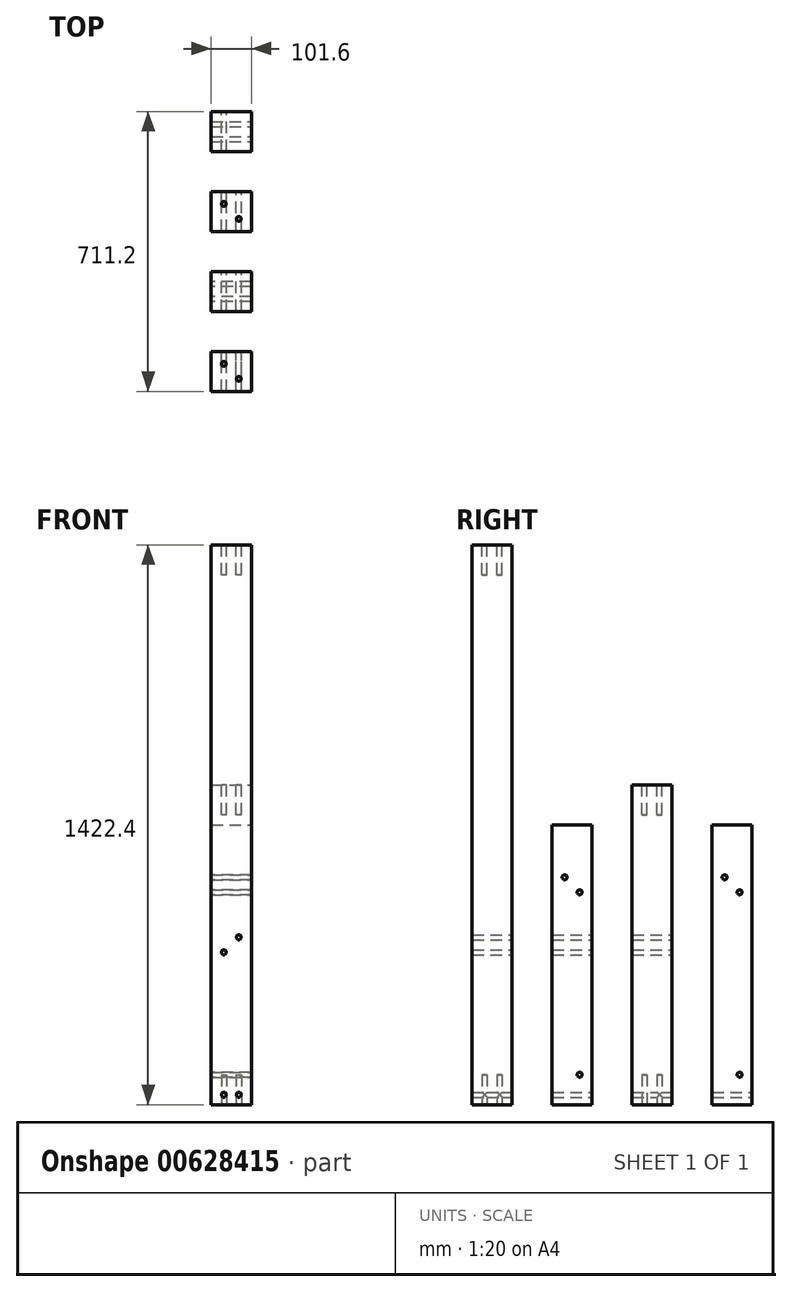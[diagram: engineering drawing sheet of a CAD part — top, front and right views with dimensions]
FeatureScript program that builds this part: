
annotation { "Feature Type Name" : "Feature", "Feature Type Description" : "" }
export const myFeature = defineFeature(function(context is Context, id is Id, definition is map)
    precondition{}
    {
        {
            var Q0;
            Q0=qCreatedBy(makeId("Top.planeOp"),FACE);
            var sketch = newSketch(context, id + "F0", { "sketchPlane" : qUnion([Q0])});
            skLineSegment(sketch, "E0", {"start": v(-50.8, 0) * mm, "end": v(50.8, 0) * mm});
            skLineSegment(sketch, "E1", {"start": v(50.8, 0) * mm, "end": v(50.8, 101.6) * mm});
            skLineSegment(sketch, "E2", {"start": v(50.8, 101.6) * mm, "end": v(-50.8, 101.6) * mm});
            skLineSegment(sketch, "E3", {"start": v(-50.8, 101.6) * mm, "end": v(-50.8, 0) * mm});
            skSolve(sketch);
        }
        {
            var Q0;
            Q0=makeQuery(id+"F0.imprint","IMPRINT",FACE,{"disambiguationData":[TD([[makeQuery(id+"F0.imprint","IMPRINT",EDGE,{"derivedFrom":sQuery(id+"F0.wireOp",EDGE,"E0")}),1.0]])]});
            extrude(context, id + "F1", {"entities" : qUnion([Q0]), "depth" : 711.2 * mm, "offsetDistance" : 25.4 * mm});
        }
        {
            var Q0;
            Q0=qCreatedBy(makeId("Top.planeOp"),FACE);
            var sketch = newSketch(context, id + "F2", { "sketchPlane" : qUnion([Q0])});
            skLineSegment(sketch, "E4", {"start": v(-50.8, -101.6) * mm, "end": v(50.8, -101.6) * mm});
            skLineSegment(sketch, "E5", {"start": v(50.8, -101.6) * mm, "end": v(50.8, -203.2) * mm});
            skLineSegment(sketch, "E6", {"start": v(50.8, -203.2) * mm, "end": v(-50.8, -203.2) * mm});
            skLineSegment(sketch, "E7", {"start": v(-50.8, -203.2) * mm, "end": v(-50.8, -101.6) * mm});
            skSolve(sketch);
        }
        {
            var Q0;
            Q0=makeQuery(id+"F2.imprint","IMPRINT",FACE,{"disambiguationData":[TD([[makeQuery(id+"F2.imprint","IMPRINT",EDGE,{"derivedFrom":sQuery(id+"F2.wireOp",EDGE,"E4")}),-1.0]])]});
            extrude(context, id + "F3", {"entities" : qUnion([Q0]), "depth" : 1422.4 * mm, "offsetDistance" : 25.4 * mm});
        }
        {
            var Q0;
            Q0=qCreatedBy(makeId("Top.planeOp"),FACE);
            var sketch = newSketch(context, id + "F4", { "sketchPlane" : qUnion([Q0])});
            skLineSegment(sketch, "E8.bottom", {"start": v(-50.8, 304.8) * mm, "end": v(50.8, 304.8) * mm});
            skLineSegment(sketch, "E8.top", {"start": v(-50.8, 203.2) * mm, "end": v(50.8, 203.2) * mm});
            skLineSegment(sketch, "E8.left", {"start": v(-50.8, 304.8) * mm, "end": v(-50.8, 203.2) * mm});
            skLineSegment(sketch, "E8.right", {"start": v(50.8, 304.8) * mm, "end": v(50.8, 203.2) * mm});
            skSolve(sketch);
        }
        {
            var Q0;
            Q0 = qSketchRegion(id + "F4", true);
            extrude(context, id + "F5", {"entities" : qUnion([Q0]), "depth" : 812.8 * mm, "offsetDistance" : 25.4 * mm});
        }
        {
            var Q0;
            Q0=makeQuery(id+"F1.opExtrude","SWEPT_FACE",FACE,{"disambiguationData":[OSD([sQuery(id+"F0.wireOp",EDGE,"E2")])]});
            var sketch = newSketch(context, id + "F6", { "sketchPlane" : qUnion([Q0])});
            skCircle(sketch, "E9", {"center": v(-19.05, 25.4) * mm, "radius": 6.35 * mm});
            skSolve(sketch);
        }
        {
            var Q0;
            Q0 = qSketchRegion(id + "F6", true);
            extrude(context, id + "F7", {"entities" : qUnion([Q0]), "operationType" : NewBodyOperationType.REMOVE, "endBound" : BoundingType.THROUGH_ALL, "oppositeDirection" : true, "depth" : 25.4 * mm, "offsetDistance" : 25.4 * mm});
        }
        {
            var Q0;
            Q0=makeQuery(id+"F1.opExtrude","SWEPT_FACE",FACE,{"disambiguationData":[OSD([sQuery(id+"F0.wireOp",EDGE,"E3")])]});
            var sketch = newSketch(context, id + "F8", { "sketchPlane" : qUnion([Q0])});
            skCircle(sketch, "E10", {"center": v(-69.85, 76.2) * mm, "radius": 6.35 * mm});
            skSolve(sketch);
        }
        {
            var Q0;
            Q0 = qSketchRegion(id + "F8", true);
            extrude(context, id + "F9", {"entities" : qUnion([Q0]), "operationType" : NewBodyOperationType.REMOVE, "endBound" : BoundingType.THROUGH_ALL, "oppositeDirection" : true, "depth" : 25.4 * mm, "offsetDistance" : 25.4 * mm});
        }
        {
            var Q0;
            Q0=makeQuery(id+"F1.opExtrude","SWEPT_FACE",FACE,{"disambiguationData":[OSD([sQuery(id+"F0.wireOp",EDGE,"E3")])]});
            var sketch = newSketch(context, id + "F10", { "sketchPlane" : qUnion([Q0])});
            skCircle(sketch, "E11", {"center": v(-31.75, 577.85) * mm, "radius": 6.35 * mm});
            skCircle(sketch, "E12", {"center": v(-69.85, 539.75) * mm, "radius": 6.35 * mm});
            skSolve(sketch);
        }
        {
            var Q0;
            Q0 = qSketchRegion(id + "F10", true);
            extrude(context, id + "F11", {"entities" : qUnion([Q0]), "operationType" : NewBodyOperationType.REMOVE, "endBound" : BoundingType.THROUGH_ALL, "oppositeDirection" : true, "depth" : 25.4 * mm, "offsetDistance" : 25.4 * mm});
        }
        {
            var Q0;
            Q0=makeQuery(id+"F3.opExtrude","CAP_FACE",FACE,{"disambiguationData":[OSD([sQuery(id+"F2.wireOp",EDGE,"E4"),sQuery(id+"F2.wireOp",EDGE,"E5"),sQuery(id+"F2.wireOp",EDGE,"E6"),sQuery(id+"F2.wireOp",EDGE,"E7")])],"isStart":true});
            var sketch = newSketch(context, id + "F12", { "sketchPlane" : qUnion([Q0])});
            skCircle(sketch, "E13", {"center": v(19.05, 171.45) * mm, "radius": 6.35 * mm});
            skCircle(sketch, "E14", {"center": v(-19.05, 133.35) * mm, "radius": 6.35 * mm});
            skSolve(sketch);
        }
        {
            var Q0;
            Q0 = qSketchRegion(id + "F12", true);
            extrude(context, id + "F13", {"entities" : qUnion([Q0]), "operationType" : NewBodyOperationType.REMOVE, "oppositeDirection" : true, "depth" : 76.2 * mm, "offsetDistance" : 25.4 * mm});
        }
        {
            var Q0;
            Q0=makeQuery(id+"F5.opExtrude","SWEPT_FACE",FACE,{"disambiguationData":[OSD([sQuery(id+"F4.wireOp",EDGE,"E8.bottom")])]});
            var sketch = newSketch(context, id + "F14", { "sketchPlane" : qUnion([Q0])});
            skPoint(sketch, "E15", {"position": v(0, 406.4) * mm});
            skPoint(sketch, "E15.positionSnap0", {"position": v(-50.8, 406.4) * mm});
            skPoint(sketch, "E15.positionSnap1", {"position": v(0, 0) * mm});
            skCircle(sketch, "E16", {"center": v(19.05, 387.35) * mm, "radius": 6.35 * mm});
            skCircle(sketch, "E17", {"center": v(-19.05, 425.45) * mm, "radius": 6.35 * mm});
            skSolve(sketch);
        }
        {
            var Q0;
            Q0 = qSketchRegion(id + "F14", true);
            extrude(context, id + "F15", {"entities" : qUnion([Q0]), "operationType" : NewBodyOperationType.REMOVE, "endBound" : BoundingType.THROUGH_ALL, "oppositeDirection" : true, "depth" : 25.4 * mm, "offsetDistance" : 25.4 * mm});
        }
        {
            var Q0;
            Q0=makeQuery(id+"F3.opExtrude","CAP_FACE",FACE,{"disambiguationData":[OSD([sQuery(id+"F2.wireOp",EDGE,"E4"),sQuery(id+"F2.wireOp",EDGE,"E5"),sQuery(id+"F2.wireOp",EDGE,"E6"),sQuery(id+"F2.wireOp",EDGE,"E7")])],"isStart":false});
            var sketch = newSketch(context, id + "F16", { "sketchPlane" : qUnion([Q0])});
            skCircle(sketch, "E18", {"center": v(-19.05, -133.35) * mm, "radius": 6.35 * mm});
            skCircle(sketch, "E19", {"center": v(19.05, -171.45) * mm, "radius": 6.35 * mm});
            skSolve(sketch);
        }
        {
            var Q0;
            Q0 = qSketchRegion(id + "F16", true);
            extrude(context, id + "F17", {"entities" : qUnion([Q0]), "operationType" : NewBodyOperationType.REMOVE, "oppositeDirection" : true, "depth" : 76.2 * mm, "offsetDistance" : 25.4 * mm});
        }
        {
            var Q0;
            Q0=makeQuery(id+"F5.opExtrude","CAP_FACE",FACE,{"disambiguationData":[OSD([sQuery(id+"F4.wireOp",EDGE,"E8.bottom"),sQuery(id+"F4.wireOp",EDGE,"E8.top"),sQuery(id+"F4.wireOp",EDGE,"E8.left"),sQuery(id+"F4.wireOp",EDGE,"E8.right")])],"isStart":false});
            var sketch = newSketch(context, id + "F18", { "sketchPlane" : qUnion([Q0])});
            skCircle(sketch, "E20", {"center": v(-19.05, 273.05) * mm, "radius": 6.35 * mm});
            skCircle(sketch, "E21", {"center": v(19.05, 234.95) * mm, "radius": 6.35 * mm});
            skSolve(sketch);
        }
        {
            var Q0;
            Q0 = qSketchRegion(id + "F18", true);
            extrude(context, id + "F19", {"entities" : qUnion([Q0]), "operationType" : NewBodyOperationType.REMOVE, "oppositeDirection" : true, "depth" : 76.2 * mm, "offsetDistance" : 25.4 * mm});
        }
        {
            var Q0;
            Q0=makeQuery(id+"F5.opExtrude","CAP_FACE",FACE,{"disambiguationData":[OSD([sQuery(id+"F4.wireOp",EDGE,"E8.bottom"),sQuery(id+"F4.wireOp",EDGE,"E8.top"),sQuery(id+"F4.wireOp",EDGE,"E8.left"),sQuery(id+"F4.wireOp",EDGE,"E8.right")])],"isStart":true});
            var sketch = newSketch(context, id + "F20", { "sketchPlane" : qUnion([Q0])});
            skCircle(sketch, "E22", {"center": v(19.05, -234.95) * mm, "radius": 6.35 * mm});
            skCircle(sketch, "E23", {"center": v(-19.05, -273.05) * mm, "radius": 6.35 * mm});
            skSolve(sketch);
        }
        {
            var Q0;
            Q0 = qSketchRegion(id + "F20", true);
            extrude(context, id + "F21", {"entities" : qUnion([Q0]), "operationType" : NewBodyOperationType.REMOVE, "oppositeDirection" : true, "depth" : 76.2 * mm, "offsetDistance" : 25.4 * mm});
        }
        {
            var Q0;
            Q0=qCreatedBy(makeId("Top.planeOp"),FACE);
            var sketch = newSketch(context, id + "F22", { "sketchPlane" : qUnion([Q0])});
            skLineSegment(sketch, "E24.bottom", {"start": v(-50.8, 508) * mm, "end": v(50.8, 508) * mm});
            skLineSegment(sketch, "E24.top", {"start": v(-50.8, 406.4) * mm, "end": v(50.8, 406.4) * mm});
            skLineSegment(sketch, "E24.left", {"start": v(-50.8, 508) * mm, "end": v(-50.8, 406.4) * mm});
            skLineSegment(sketch, "E24.right", {"start": v(50.8, 508) * mm, "end": v(50.8, 406.4) * mm});
            skSolve(sketch);
        }
        {
            var Q0;
            Q0 = qSketchRegion(id + "F22", true);
            extrude(context, id + "F23", {"entities" : qUnion([Q0]), "depth" : 711.2 * mm, "offsetDistance" : 25.4 * mm});
        }
        {
            var Q0;
            Q0=makeQuery(id+"F23.opExtrude","SWEPT_FACE",FACE,{"disambiguationData":[OSD([sQuery(id+"F22.wireOp",EDGE,"E24.right")])]});
            var sketch = newSketch(context, id + "F24", { "sketchPlane" : qUnion([Q0])});
            skCircle(sketch, "E25", {"center": v(476.25, 539.75) * mm, "radius": 6.35 * mm});
            skCircle(sketch, "E26", {"center": v(438.15, 577.85) * mm, "radius": 6.35 * mm});
            skSolve(sketch);
        }
        {
            var Q0;
            Q0 = qSketchRegion(id + "F24", true);
            extrude(context, id + "F25", {"entities" : qUnion([Q0]), "operationType" : NewBodyOperationType.REMOVE, "endBound" : BoundingType.THROUGH_ALL, "oppositeDirection" : true, "depth" : 25.4 * mm, "offsetDistance" : 25.4 * mm});
        }
        {
            var Q0;
            Q0=makeQuery(id+"F23.opExtrude","SWEPT_FACE",FACE,{"disambiguationData":[OSD([sQuery(id+"F22.wireOp",EDGE,"E24.bottom")])]});
            var sketch = newSketch(context, id + "F26", { "sketchPlane" : qUnion([Q0])});
            skCircle(sketch, "E27", {"center": v(19.05, 25.4) * mm, "radius": 6.35 * mm});
            skSolve(sketch);
        }
        {
            var Q0;
            Q0 = qSketchRegion(id + "F26", true);
            extrude(context, id + "F27", {"entities" : qUnion([Q0]), "operationType" : NewBodyOperationType.REMOVE, "endBound" : BoundingType.THROUGH_ALL, "oppositeDirection" : true, "depth" : 25.4 * mm, "offsetDistance" : 25.4 * mm});
        }
        {
            var Q0;
            Q0=makeQuery(id+"F23.opExtrude","SWEPT_FACE",FACE,{"disambiguationData":[OSD([sQuery(id+"F22.wireOp",EDGE,"E24.right")])]});
            var sketch = newSketch(context, id + "F28", { "sketchPlane" : qUnion([Q0])});
            skCircle(sketch, "E28", {"center": v(476.25, 76.2) * mm, "radius": 6.35 * mm});
            skSolve(sketch);
        }
        {
            var Q0;
            Q0 = qSketchRegion(id + "F28", true);
            extrude(context, id + "F29", {"entities" : qUnion([Q0]), "operationType" : NewBodyOperationType.REMOVE, "endBound" : BoundingType.THROUGH_ALL, "oppositeDirection" : true, "depth" : 25.4 * mm, "offsetDistance" : 25.4 * mm});
        }
    });
